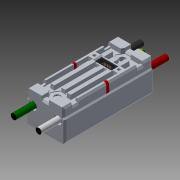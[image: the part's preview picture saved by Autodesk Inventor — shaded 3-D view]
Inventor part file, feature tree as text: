
AUTODESK INVENTOR PART (.ipt)
format: ipt  version: 2018 (Build 220112000, 112)  size: 3,541,504 bytes
history: native  units: in
note: dims shown in document units (in); Inventor stores cm internally (conversion verified against a paired STEP export)
features: plane x2, split x2, boolean_combine x1, imported_body x1
ambient origin geometry x8: Origin, YZ Plane, XZ Plane, XY Plane, X Axis, Y Axis, Z Axis, Center Point
bodies: Body1 (feature_tree)
feature tree (6):
  boolean_combine  "Combine11"
  plane  "Work Plane1"
  split  "Split1"
  plane  "Work Plane2"
  split  "Split2"
  imported_body  "Base1"
